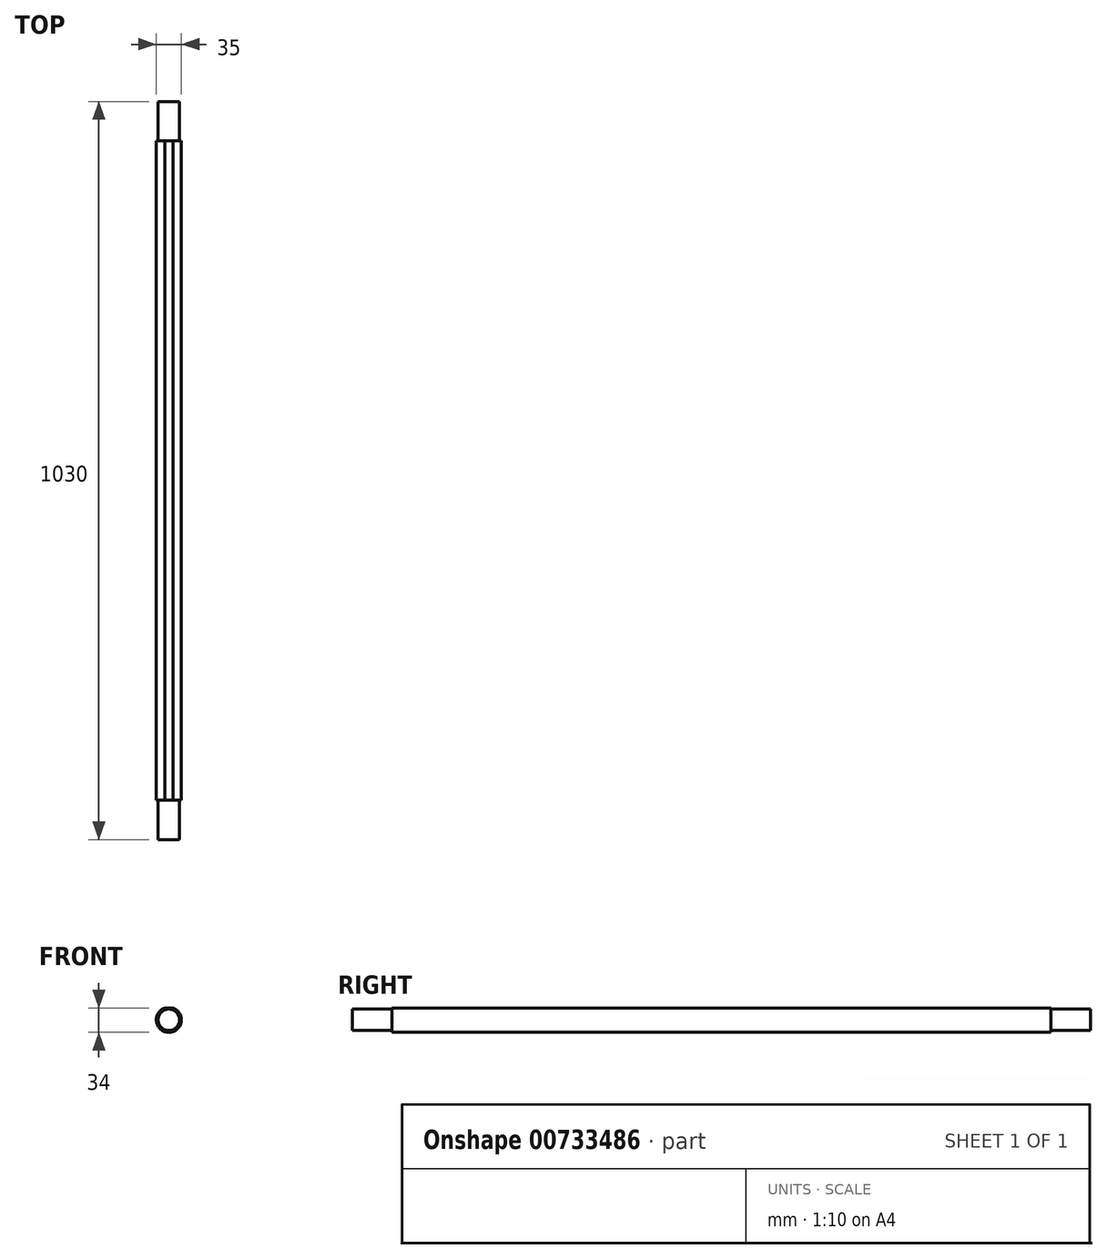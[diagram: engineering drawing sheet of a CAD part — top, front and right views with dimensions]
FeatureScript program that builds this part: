
annotation { "Feature Type Name" : "Feature", "Feature Type Description" : "" }
export const myFeature = defineFeature(function(context is Context, id is Id, definition is map)
    precondition{}
    {
        {
            var Q0;
            Q0=qCreatedBy(makeId("Front.planeOp"),FACE);
            var sketch = newSketch(context, id + "F0", { "sketchPlane" : qUnion([Q0])});
            skArc(sketch, "E0", {"start": v(-5.83, 16.5) * mm, "mid": v(0, -17.5) * mm, "end": v(5.83, 16.5) * mm});
            skLineSegment(sketch, "E1", {"start": v(-5.83, 16.5) * mm, "end": v(5.83, 16.5) * mm});
            skSolve(sketch);
        }
        {
            var Q0;
            Q0 = qSketchRegion(id + "F0", true);
            extrude(context, id + "F1", {"entities" : qUnion([Q0]), "depth" : 1030 * mm, "offsetDistance" : 25 * mm});
        }
        {
            var Q0;
            Q0=qCreatedBy(makeId("Front.planeOp"),FACE);
            var sketch = newSketch(context, id + "F2", { "sketchPlane" : qUnion([Q0])});
            skCircle(sketch, "E2", {"center": v(0, 0) * mm, "radius": 15 * mm});
            skCircle(sketch, "E3", {"center": v(0, 0) * mm, "radius": 17.5 * mm});
            skSolve(sketch);
        }
        {
            var Q0;
            Q0 = qSketchRegion(id + "F2", true);
            extrude(context, id + "F3", {"entities" : qUnion([Q0]), "operationType" : NewBodyOperationType.REMOVE, "depth" : 55 * mm, "offsetDistance" : 25 * mm});
        }
        {
            var Q0;
            Q0=makeQuery(id+"F1.opExtrude","CAP_FACE",FACE,{"disambiguationData":[OSD([sQuery(id+"F0.wireOp",EDGE,"E0"),sQuery(id+"F0.wireOp",EDGE,"E1")])],"isStart":false});
            var sketch = newSketch(context, id + "F4", { "sketchPlane" : qUnion([Q0])});
            skCircle(sketch, "E4", {"center": v(0, 0) * mm, "radius": 17.5 * mm});
            skCircle(sketch, "E5", {"center": v(0, 0) * mm, "radius": 15 * mm});
            skSolve(sketch);
        }
        {
            var Q0;
            Q0 = qSketchRegion(id + "F4", true);
            extrude(context, id + "F5", {"entities" : qUnion([Q0]), "operationType" : NewBodyOperationType.REMOVE, "oppositeDirection" : true, "depth" : 55 * mm, "offsetDistance" : 25 * mm});
        }
    });
